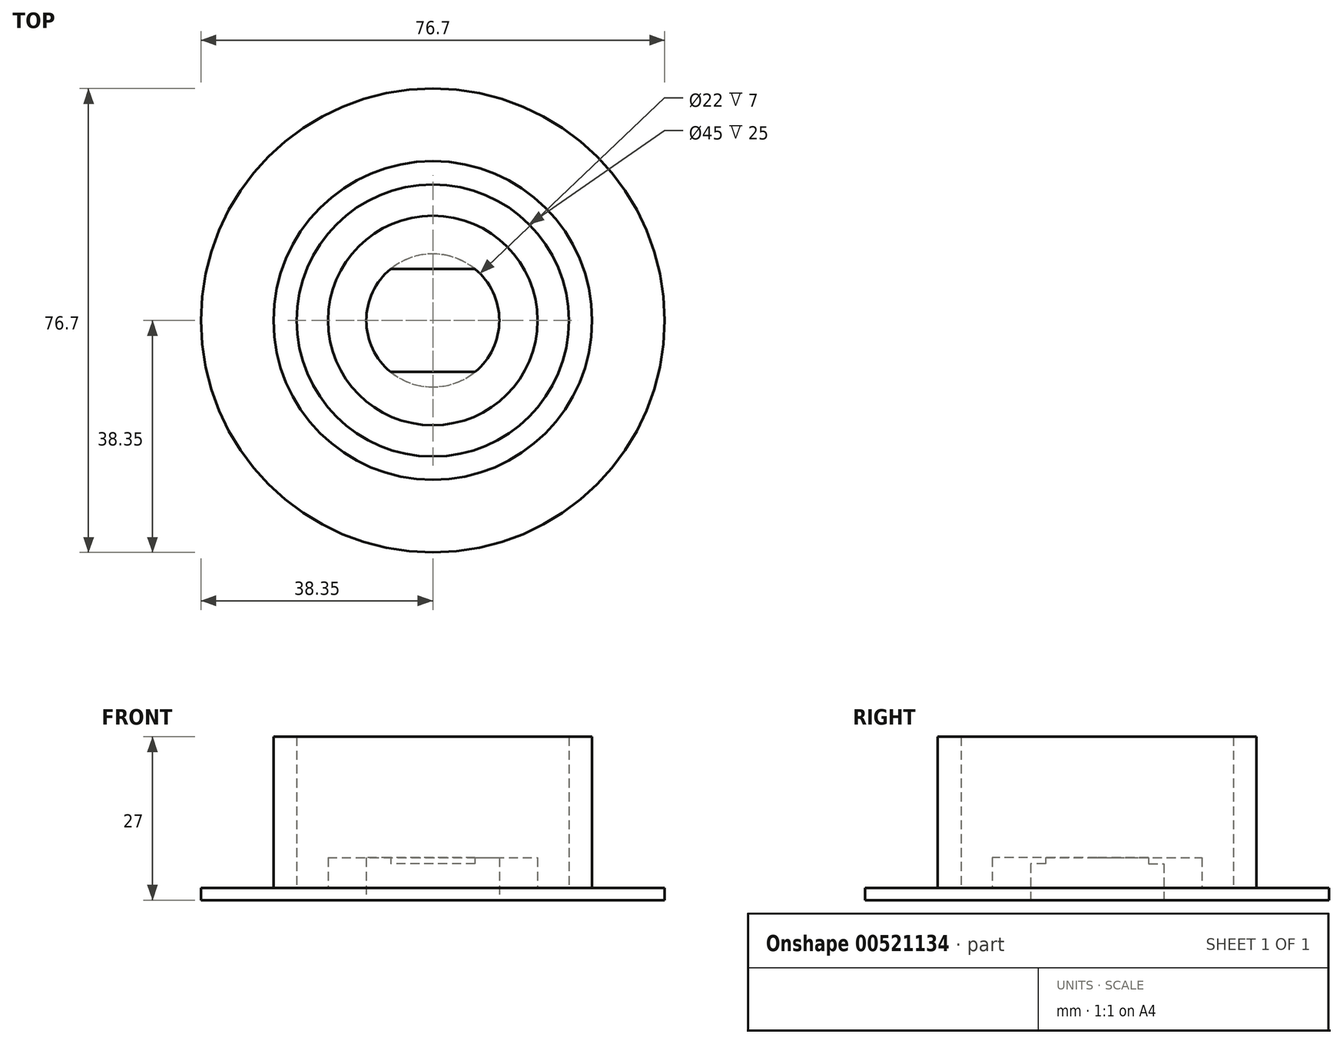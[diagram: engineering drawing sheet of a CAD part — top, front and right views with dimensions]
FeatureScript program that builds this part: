
annotation { "Feature Type Name" : "Feature", "Feature Type Description" : "" }
export const myFeature = defineFeature(function(context is Context, id is Id, definition is map)
    precondition{}
    {
        {
            var Q0;
            Q0=qCreatedBy(makeId("Top.planeOp"),FACE);
            var sketch = newSketch(context, id + "F0", { "sketchPlane" : qUnion([Q0])});
            skCircle(sketch, "E0", {"center": v(0, 0) * mm, "radius": 26.35 * mm});
            skCircle(sketch, "E1", {"center": v(0, 0) * mm, "radius": 22.5 * mm});
            skSolve(sketch);
        }
        {
            var Q0;
            Q0=makeQuery(id+"F0.imprint","IMPRINT",FACE,{"disambiguationData":[TD([[makeQuery(id+"F0.imprint","IMPRINT",EDGE,{"derivedFrom":sQuery(id+"F0.wireOp",EDGE,"E0")}),1.0]])]});
            extrude(context, id + "F1", {"entities" : qUnion([Q0]), "depth" : 25 * mm, "offsetDistance" : 25 * mm});
        }
        {
            var Q0;
            Q0=makeQuery(id+"F1.opExtrude","CAP_FACE",FACE,{"disambiguationData":[OSD([sQuery(id+"F0.wireOp",EDGE,"E0"),sQuery(id+"F0.wireOp",EDGE,"E1")])],"isStart":true});
            var sketch = newSketch(context, id + "F2", { "sketchPlane" : qUnion([Q0])});
            skCircle(sketch, "E2", {"center": v(0, 0) * mm, "radius": 38.35 * mm});
            skSolve(sketch);
        }
        {
            var Q0;
            Q0=makeQuery(id+"F2.imprint","IMPRINT",FACE,{"disambiguationData":[TD([[makeQuery(id+"F2.imprint","IMPRINT",EDGE,{"derivedFrom":sQuery(id+"F2.wireOp",EDGE,"E2")}),1.0]])]});
            var Q1;
            Q1=makeQuery(id+"F2.imprint","IMPRINT",FACE,{"disambiguationData":[TD([[makeQuery(id+"F2.imprint","IMPRINT",EDGE,{"derivedFrom":makeQuery(id+"F1.opExtrude","CAP_EDGE",EDGE,{"disambiguationData":[OSD([sQuery(id+"F0.wireOp",EDGE,"E0")])],"isStart":true})}),-1.0]])]});
            var Q2;
            Q2=makeQuery(id+"F2.imprint","IMPRINT",FACE,{"disambiguationData":[TD([[makeQuery(id+"F2.imprint","IMPRINT",EDGE,{"derivedFrom":makeQuery(id+"F1.opExtrude","CAP_EDGE",EDGE,{"disambiguationData":[OSD([sQuery(id+"F0.wireOp",EDGE,"E1")])],"isStart":true})}),-1.0]])]});
            extrude(context, id + "F3", {"entities" : qUnion([Q0, Q1, Q2]), "operationType" : NewBodyOperationType.ADD, "depth" : 2 * mm, "offsetDistance" : 25 * mm});
        }
        {
            var Q0;
            Q0=makeQuery(id+"F3.opExtrude","CAP_FACE",FACE,{"disambiguationData":[OSD([sQuery(id+"F2.wireOp",EDGE,"E2")])],"isStart":false});
            var sketch = newSketch(context, id + "F4", { "sketchPlane" : qUnion([Q0])});
            skCircle(sketch, "E3", {"center": v(0, 0) * mm, "radius": 11 * mm});
            skSolve(sketch);
        }
        {
            var Q0;
            Q0=makeQuery(id+"F4.imprint","IMPRINT",FACE,{"disambiguationData":[TD([[makeQuery(id+"F4.imprint","IMPRINT",EDGE,{"derivedFrom":sQuery(id+"F4.wireOp",EDGE,"E3")}),1.0]])]});
            extrude(context, id + "F5", {"entities" : qUnion([Q0]), "operationType" : NewBodyOperationType.REMOVE, "oppositeDirection" : true, "depth" : 25 * mm, "offsetDistance" : 25 * mm});
        }
        {
            var Q0;
            Q0=makeQuery(id+"F3.boolean.opBoolean","SPLIT",FACE,{"disambiguationData":[TD([makeQuery(id+"F1.opExtrude","SWEPT_FACE",FACE,{"disambiguationData":[OSD([sQuery(id+"F0.wireOp",EDGE,"E1")])]})])],"derivedFrom":makeQuery(id+"F3.opExtrude","CAP_FACE",FACE,{"disambiguationData":[OSD([sQuery(id+"F2.wireOp",EDGE,"E2")])],"isStart":true})});
            var sketch = newSketch(context, id + "F6", { "sketchPlane" : qUnion([Q0])});
            skCircle(sketch, "E4", {"center": v(0, 0) * mm, "radius": 17.33 * mm});
            skSolve(sketch);
        }
        {
            var Q0;
            Q0 = qSketchRegion(id + "F6", true);
            extrude(context, id + "F7", {"entities" : qUnion([Q0]), "operationType" : NewBodyOperationType.ADD, "depth" : 5 * mm, "offsetDistance" : 25 * mm});
        }
        {
            var Q0;
            Q0=makeQuery(id+"F7.opExtrude","CAP_FACE",FACE,{"disambiguationData":[OSD([sQuery(id+"F6.wireOp",EDGE,"E4")])],"isStart":true});
            var sketch = newSketch(context, id + "F8", { "sketchPlane" : qUnion([Q0])});
            skCircle(sketch, "E5", {"center": v(0, 0) * mm, "radius": 11 * mm});
            skSolve(sketch);
        }
        {
            var Q0;
            Q0 = qSketchRegion(id + "F8", true);
            extrude(context, id + "F9", {"entities" : qUnion([Q0]), "operationType" : NewBodyOperationType.REMOVE, "oppositeDirection" : true, "depth" : 25 * mm, "offsetDistance" : 25 * mm});
        }
        {
            var Q0;
            Q0=makeQuery(id+"F7.opExtrude","CAP_FACE",FACE,{"disambiguationData":[OSD([sQuery(id+"F6.wireOp",EDGE,"E4")])],"isStart":false});
            var sketch = newSketch(context, id + "F10", { "sketchPlane" : qUnion([Q0])});
            skLineSegment(sketch, "E6.bottom", {"start": v(10.7, 11.5) * mm, "end": v(-9.03, 11.5) * mm});
            skLineSegment(sketch, "E6.top", {"start": v(10.7, 8.5) * mm, "end": v(-9.03, 8.5) * mm});
            skLineSegment(sketch, "E6.left", {"start": v(10.7, 11.5) * mm, "end": v(10.7, 8.5) * mm});
            skLineSegment(sketch, "E6.right", {"start": v(-9.03, 11.5) * mm, "end": v(-9.03, 8.5) * mm});
            skLineSegment(sketch, "E7.bottom", {"start": v(11.2, -11.5) * mm, "end": v(-10.35, -11.5) * mm});
            skLineSegment(sketch, "E7.top", {"start": v(11.2, -8.5) * mm, "end": v(-10.35, -8.5) * mm});
            skLineSegment(sketch, "E7.left", {"start": v(11.2, -11.5) * mm, "end": v(11.2, -8.5) * mm});
            skLineSegment(sketch, "E7.right", {"start": v(-10.35, -11.5) * mm, "end": v(-10.35, -8.5) * mm});
            skSolve(sketch);
        }
        {
            var Q0;
            Q0 = qSketchRegion(id + "F10", true);
            extrude(context, id + "F11", {"entities" : qUnion([Q0]), "operationType" : NewBodyOperationType.ADD, "oppositeDirection" : true, "depth" : 1 * mm, "offsetDistance" : 25 * mm});
        }
    });
